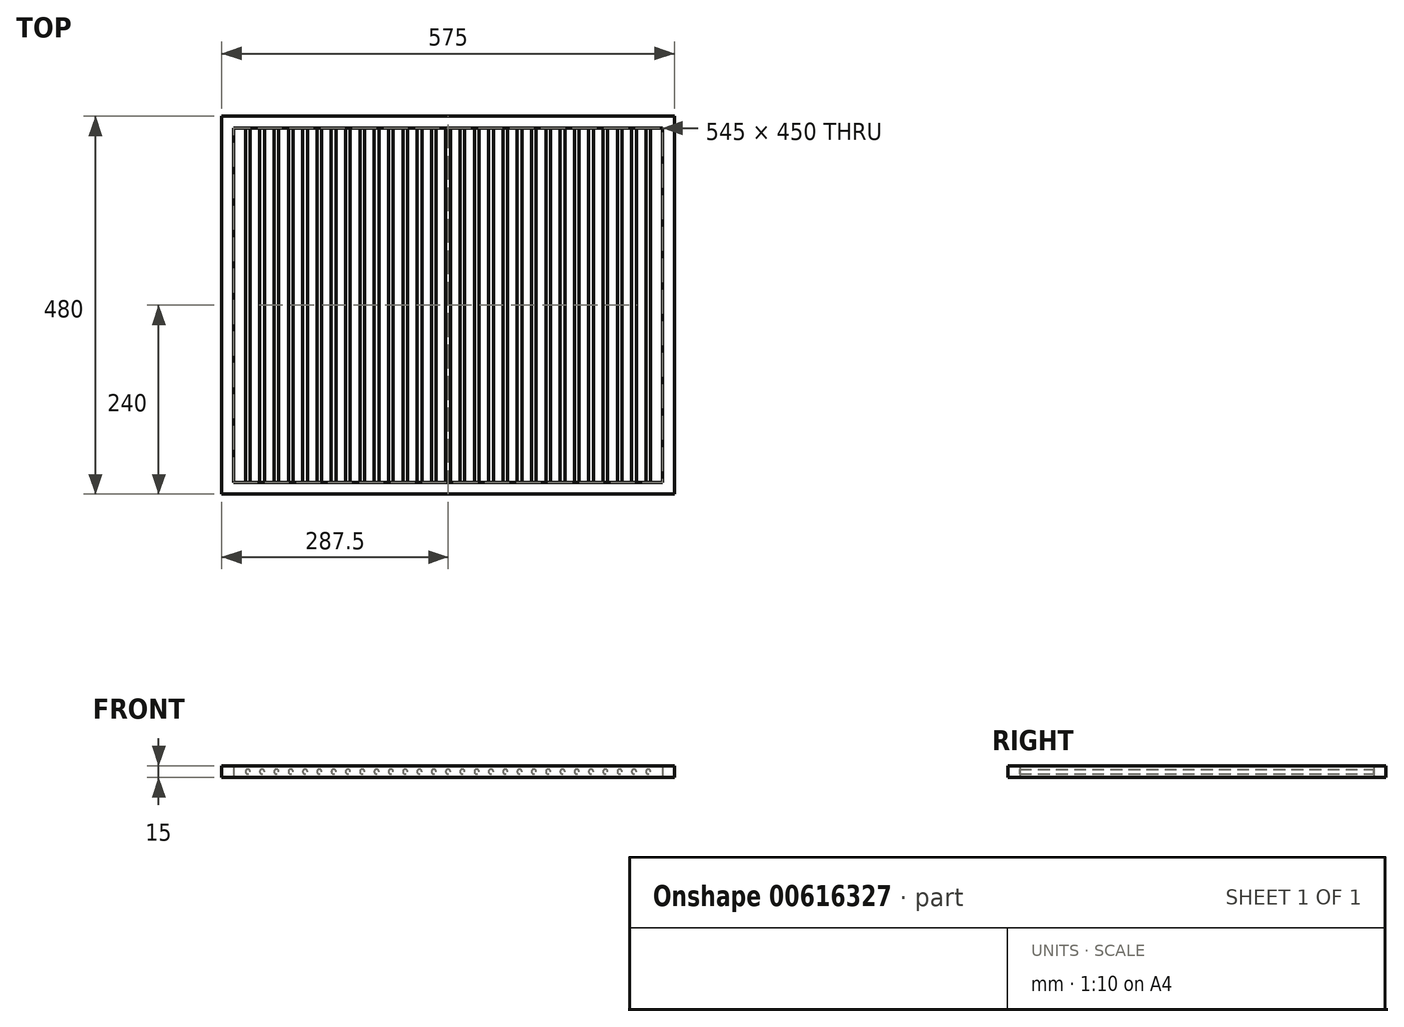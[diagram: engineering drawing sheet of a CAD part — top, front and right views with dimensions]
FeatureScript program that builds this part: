
annotation { "Feature Type Name" : "Feature", "Feature Type Description" : "" }
export const myFeature = defineFeature(function(context is Context, id is Id, definition is map)
    precondition{}
    {
        {
            var Q0;
            Q0=qCreatedBy(makeId("Top.planeOp"),FACE);
            var sketch = newSketch(context, id + "F0", { "sketchPlane" : qUnion([Q0])});
            skLineSegment(sketch, "E0.bottom", {"start": v(0, 465) * mm, "end": v(560, 465) * mm});
            skLineSegment(sketch, "E0.top", {"start": v(0, 0) * mm, "end": v(560, 0) * mm});
            skLineSegment(sketch, "E0.left", {"start": v(0, 465) * mm, "end": v(0, 0) * mm});
            skLineSegment(sketch, "E0.right", {"start": v(560, 465) * mm, "end": v(560, 0) * mm});
            skLineSegment(sketch, "E1.bottom", {"start": v(0, -1254.37) * mm, "end": v(0, -1254.37) * mm});
            skLineSegment(sketch, "E1.top", {"start": v(0, -1274.55) * mm, "end": v(0, -1274.55) * mm});
            skSolve(sketch);
        }
        {
            var Q0;
            Q0=qCreatedBy(makeId("Right.planeOp"),FACE);
            var sketch = newSketch(context, id + "F1", { "sketchPlane" : qUnion([Q0])});
            skLineSegment(sketch, "E2.bottom", {"start": v(-7.5, 7.5) * mm, "end": v(7.5, 7.5) * mm});
            skLineSegment(sketch, "E2.top", {"start": v(-7.5, -7.5) * mm, "end": v(7.5, -7.5) * mm});
            skLineSegment(sketch, "E2.left", {"start": v(-7.5, 7.5) * mm, "end": v(-7.5, -7.5) * mm});
            skLineSegment(sketch, "E2.right", {"start": v(7.5, 7.5) * mm, "end": v(7.5, -7.5) * mm});
            skPoint(sketch, "E2.middle", {"position": v(0, 0) * mm});
            skSolve(sketch);
        }
        {
            var Q0;
            Q0=makeQuery(id+"F1.imprint","IMPRINT",FACE,{"disambiguationData":[TD([[makeQuery(id+"F1.imprint","IMPRINT",EDGE,{"derivedFrom":sQuery(id+"F1.wireOp",EDGE,"E2.bottom")}),-1.0]])]});
            var Q1;
            Q1=sQuery(id+"F0.wireOp",EDGE,"E0.top");
            var Q2;
            Q2=sQuery(id+"F0.wireOp",EDGE,"E0.right");
            var Q3;
            Q3=sQuery(id+"F0.wireOp",EDGE,"E0.bottom");
            var Q4;
            Q4=sQuery(id+"F0.wireOp",EDGE,"E0.left");
            sweep(context, id + "F2", {"profiles" : qUnion([Q0]), "path" : qUnion([Q1, Q2, Q3, Q4])});
        }
        {
            var Q0;
            Q0=makeQuery(id+"F2.opSweep","SWEPT_FACE",FACE,{"disambiguationData":[OSD([sQuery(id+"F0.wireOp",EDGE,"E0.bottom"),sQuery(id+"F1.wireOp",EDGE,"E2.right")])]});
            var sketch = newSketch(context, id + "F3", { "sketchPlane" : qUnion([Q0])});
            skCircle(sketch, "E3", {"center": v(25.67, 0) * mm, "radius": 3 * mm});
            skCircle(sketch, "E4.1.0.0", {"center": v(43.83, 0) * mm, "radius": 3 * mm});
            skCircle(sketch, "E4.2.0.0", {"center": v(62, 0) * mm, "radius": 3 * mm});
            skCircle(sketch, "E4.3.0.0", {"center": v(80.17, 0) * mm, "radius": 3 * mm});
            skCircle(sketch, "E4.4.0.0", {"center": v(98.33, 0) * mm, "radius": 3 * mm});
            skCircle(sketch, "E4.5.0.0", {"center": v(116.5, 0) * mm, "radius": 3 * mm});
            skCircle(sketch, "E4.6.0.0", {"center": v(134.67, 0) * mm, "radius": 3 * mm});
            skCircle(sketch, "E4.7.0.0", {"center": v(152.83, 0) * mm, "radius": 3 * mm});
            skCircle(sketch, "E4.8.0.0", {"center": v(171, 0) * mm, "radius": 3 * mm});
            skCircle(sketch, "E4.9.0.0", {"center": v(189.17, 0) * mm, "radius": 3 * mm});
            skCircle(sketch, "E4.10.0.0", {"center": v(207.33, 0) * mm, "radius": 3 * mm});
            skCircle(sketch, "E4.11.0.0", {"center": v(225.5, 0) * mm, "radius": 3 * mm});
            skCircle(sketch, "E4.12.0.0", {"center": v(243.67, 0) * mm, "radius": 3 * mm});
            skCircle(sketch, "E4.13.0.0", {"center": v(261.83, 0) * mm, "radius": 3 * mm});
            skCircle(sketch, "E4.14.0.0", {"center": v(280, 0) * mm, "radius": 3 * mm});
            skCircle(sketch, "E4.15.0.0", {"center": v(298.17, 0) * mm, "radius": 3 * mm});
            skCircle(sketch, "E4.16.0.0", {"center": v(316.33, 0) * mm, "radius": 3 * mm});
            skLineSegment(sketch, "E4.direction1", {"start": v(25.67, 0) * mm, "end": v(43.83, 0) * mm, "construction": true});
            skCircle(sketch, "E5.0.17.0", {"center": v(334.5, 0) * mm, "radius": 3 * mm});
            skCircle(sketch, "E6.0.18.0", {"center": v(352.67, 0) * mm, "radius": 3 * mm});
            skCircle(sketch, "E7.0.19.0", {"center": v(370.83, 0) * mm, "radius": 3 * mm});
            skCircle(sketch, "E7.0.20.0", {"center": v(389, 0) * mm, "radius": 3 * mm});
            skCircle(sketch, "E7.0.21.0", {"center": v(407.17, 0) * mm, "radius": 3 * mm});
            skCircle(sketch, "E7.0.22.0", {"center": v(425.33, 0) * mm, "radius": 3 * mm});
            skCircle(sketch, "E7.0.23.0", {"center": v(443.5, 0) * mm, "radius": 3 * mm});
            skCircle(sketch, "E7.0.24.0", {"center": v(461.67, 0) * mm, "radius": 3 * mm});
            skCircle(sketch, "E7.0.25.0", {"center": v(479.83, 0) * mm, "radius": 3 * mm});
            skCircle(sketch, "E7.0.26.0", {"center": v(498, 0) * mm, "radius": 3 * mm});
            skCircle(sketch, "E7.0.27.0", {"center": v(516.17, 0) * mm, "radius": 3 * mm});
            skCircle(sketch, "E7.0.28.0", {"center": v(534.33, 0) * mm, "radius": 3 * mm});
            skSolve(sketch);
        }
        {
            var Q0;
            Q0=makeQuery(id+"F3.imprint","IMPRINT",FACE,{"disambiguationData":[TD([[makeQuery(id+"F3.imprint","IMPRINT",EDGE,{"derivedFrom":sQuery(id+"F3.wireOp",EDGE,"E3")}),1.0]])]});
            var Q1;
            Q1=makeQuery(id+"F3.imprint","IMPRINT",FACE,{"disambiguationData":[TD([[makeQuery(id+"F3.imprint","IMPRINT",EDGE,{"derivedFrom":sQuery(id+"F3.wireOp",EDGE,"E4.1.0.0")}),1.0]])]});
            var Q2;
            Q2=makeQuery(id+"F3.imprint","IMPRINT",FACE,{"disambiguationData":[TD([[makeQuery(id+"F3.imprint","IMPRINT",EDGE,{"derivedFrom":sQuery(id+"F3.wireOp",EDGE,"E4.2.0.0")}),1.0]])]});
            var Q3;
            Q3=makeQuery(id+"F3.imprint","IMPRINT",FACE,{"disambiguationData":[TD([[makeQuery(id+"F3.imprint","IMPRINT",EDGE,{"derivedFrom":sQuery(id+"F3.wireOp",EDGE,"E4.3.0.0")}),1.0]])]});
            var Q4;
            Q4=makeQuery(id+"F3.imprint","IMPRINT",FACE,{"disambiguationData":[TD([[makeQuery(id+"F3.imprint","IMPRINT",EDGE,{"derivedFrom":sQuery(id+"F3.wireOp",EDGE,"E4.4.0.0")}),1.0]])]});
            var Q5;
            Q5=makeQuery(id+"F3.imprint","IMPRINT",FACE,{"disambiguationData":[TD([[makeQuery(id+"F3.imprint","IMPRINT",EDGE,{"derivedFrom":sQuery(id+"F3.wireOp",EDGE,"E4.5.0.0")}),1.0]])]});
            var Q6;
            Q6=makeQuery(id+"F3.imprint","IMPRINT",FACE,{"disambiguationData":[TD([[makeQuery(id+"F3.imprint","IMPRINT",EDGE,{"derivedFrom":sQuery(id+"F3.wireOp",EDGE,"E4.6.0.0")}),1.0]])]});
            var Q7;
            Q7=makeQuery(id+"F3.imprint","IMPRINT",FACE,{"disambiguationData":[TD([[makeQuery(id+"F3.imprint","IMPRINT",EDGE,{"derivedFrom":sQuery(id+"F3.wireOp",EDGE,"E4.7.0.0")}),1.0]])]});
            var Q8;
            Q8=makeQuery(id+"F3.imprint","IMPRINT",FACE,{"disambiguationData":[TD([[makeQuery(id+"F3.imprint","IMPRINT",EDGE,{"derivedFrom":sQuery(id+"F3.wireOp",EDGE,"E4.8.0.0")}),1.0]])]});
            var Q9;
            Q9=makeQuery(id+"F3.imprint","IMPRINT",FACE,{"disambiguationData":[TD([[makeQuery(id+"F3.imprint","IMPRINT",EDGE,{"derivedFrom":sQuery(id+"F3.wireOp",EDGE,"E4.9.0.0")}),1.0]])]});
            var Q10;
            Q10=makeQuery(id+"F3.imprint","IMPRINT",FACE,{"disambiguationData":[TD([[makeQuery(id+"F3.imprint","IMPRINT",EDGE,{"derivedFrom":sQuery(id+"F3.wireOp",EDGE,"E4.10.0.0")}),1.0]])]});
            var Q11;
            Q11=makeQuery(id+"F3.imprint","IMPRINT",FACE,{"disambiguationData":[TD([[makeQuery(id+"F3.imprint","IMPRINT",EDGE,{"derivedFrom":sQuery(id+"F3.wireOp",EDGE,"E4.11.0.0")}),1.0]])]});
            var Q12;
            Q12=makeQuery(id+"F3.imprint","IMPRINT",FACE,{"disambiguationData":[TD([[makeQuery(id+"F3.imprint","IMPRINT",EDGE,{"derivedFrom":sQuery(id+"F3.wireOp",EDGE,"E4.12.0.0")}),1.0]])]});
            var Q13;
            Q13=makeQuery(id+"F3.imprint","IMPRINT",FACE,{"disambiguationData":[TD([[makeQuery(id+"F3.imprint","IMPRINT",EDGE,{"derivedFrom":sQuery(id+"F3.wireOp",EDGE,"E4.13.0.0")}),1.0]])]});
            var Q14;
            Q14=makeQuery(id+"F3.imprint","IMPRINT",FACE,{"disambiguationData":[TD([[makeQuery(id+"F3.imprint","IMPRINT",EDGE,{"derivedFrom":sQuery(id+"F3.wireOp",EDGE,"E4.14.0.0")}),1.0]])]});
            var Q15;
            Q15=makeQuery(id+"F3.imprint","IMPRINT",FACE,{"disambiguationData":[TD([[makeQuery(id+"F3.imprint","IMPRINT",EDGE,{"derivedFrom":sQuery(id+"F3.wireOp",EDGE,"E4.15.0.0")}),1.0]])]});
            var Q16;
            Q16=makeQuery(id+"F3.imprint","IMPRINT",FACE,{"disambiguationData":[TD([[makeQuery(id+"F3.imprint","IMPRINT",EDGE,{"derivedFrom":sQuery(id+"F3.wireOp",EDGE,"E4.16.0.0")}),1.0]])]});
            var Q17;
            Q17=makeQuery(id+"F3.imprint","IMPRINT",FACE,{"disambiguationData":[TD([[makeQuery(id+"F3.imprint","IMPRINT",EDGE,{"derivedFrom":sQuery(id+"F3.wireOp",EDGE,"E5.0.17.0")}),1.0]])]});
            var Q18;
            Q18=makeQuery(id+"F3.imprint","IMPRINT",FACE,{"disambiguationData":[TD([[makeQuery(id+"F3.imprint","IMPRINT",EDGE,{"derivedFrom":sQuery(id+"F3.wireOp",EDGE,"E6.0.18.0")}),1.0]])]});
            var Q19;
            Q19=makeQuery(id+"F3.imprint","IMPRINT",FACE,{"disambiguationData":[TD([[makeQuery(id+"F3.imprint","IMPRINT",EDGE,{"derivedFrom":sQuery(id+"F3.wireOp",EDGE,"E7.0.19.0")}),1.0]])]});
            var Q20;
            Q20=makeQuery(id+"F3.imprint","IMPRINT",FACE,{"disambiguationData":[TD([[makeQuery(id+"F3.imprint","IMPRINT",EDGE,{"derivedFrom":sQuery(id+"F3.wireOp",EDGE,"E7.0.20.0")}),1.0]])]});
            var Q21;
            Q21=makeQuery(id+"F3.imprint","IMPRINT",FACE,{"disambiguationData":[TD([[makeQuery(id+"F3.imprint","IMPRINT",EDGE,{"derivedFrom":sQuery(id+"F3.wireOp",EDGE,"E7.0.21.0")}),1.0]])]});
            var Q22;
            Q22=makeQuery(id+"F3.imprint","IMPRINT",FACE,{"disambiguationData":[TD([[makeQuery(id+"F3.imprint","IMPRINT",EDGE,{"derivedFrom":sQuery(id+"F3.wireOp",EDGE,"E7.0.22.0")}),1.0]])]});
            var Q23;
            Q23=makeQuery(id+"F3.imprint","IMPRINT",FACE,{"disambiguationData":[TD([[makeQuery(id+"F3.imprint","IMPRINT",EDGE,{"derivedFrom":sQuery(id+"F3.wireOp",EDGE,"E7.0.23.0")}),1.0]])]});
            var Q24;
            Q24=makeQuery(id+"F3.imprint","IMPRINT",FACE,{"disambiguationData":[TD([[makeQuery(id+"F3.imprint","IMPRINT",EDGE,{"derivedFrom":sQuery(id+"F3.wireOp",EDGE,"E7.0.24.0")}),1.0]])]});
            var Q25;
            Q25=makeQuery(id+"F3.imprint","IMPRINT",FACE,{"disambiguationData":[TD([[makeQuery(id+"F3.imprint","IMPRINT",EDGE,{"derivedFrom":sQuery(id+"F3.wireOp",EDGE,"E7.0.25.0")}),1.0]])]});
            var Q26;
            Q26=makeQuery(id+"F3.imprint","IMPRINT",FACE,{"disambiguationData":[TD([[makeQuery(id+"F3.imprint","IMPRINT",EDGE,{"derivedFrom":sQuery(id+"F3.wireOp",EDGE,"E7.0.26.0")}),1.0]])]});
            var Q27;
            Q27=makeQuery(id+"F3.imprint","IMPRINT",FACE,{"disambiguationData":[TD([[makeQuery(id+"F3.imprint","IMPRINT",EDGE,{"derivedFrom":sQuery(id+"F3.wireOp",EDGE,"E7.0.27.0")}),1.0]])]});
            var Q28;
            Q28=makeQuery(id+"F3.imprint","IMPRINT",FACE,{"disambiguationData":[TD([[makeQuery(id+"F3.imprint","IMPRINT",EDGE,{"derivedFrom":sQuery(id+"F3.wireOp",EDGE,"E7.0.28.0")}),1.0]])]});
            extrude(context, id + "F4", {"entities" : qUnion([Q0, Q1, Q2, Q3, Q4, Q5, Q6, Q7, Q8, Q9, Q10, Q11, Q12, Q13, Q14, Q15, Q16, Q17, Q18, Q19, Q20, Q21, Q22, Q23, Q24, Q25, Q26, Q27, Q28]), "operationType" : NewBodyOperationType.ADD, "depth" : 450 * mm, "offsetDistance" : 25 * mm});
        }
    });
